# Revit family: QF_BOURGEAT_Self_Bain_marie_air_5GN
name_source: partatom
category: Equipement spécialisé
revit_build: Autodesk Revit 2015 (Build: 20140606_1530(x64)
units: mm (PartAtom-declared; Revit-internal decimal feet)

## types (18) — shared parameters
Certification = NF alimentaire
Charge max = 200.00 kg
Cuve à air = Oui
Cuve à eau = Non
Fabricant = BOURGEAT
Fréquence = 50 Hz
Indice de protection = 21
Longueur hors tout = 1859 mm  [stored 6.09908 ft]
Nature isolant = Laine de verre
Phase = 2
Profondeur hors tout = 820 mm  [stored 2.69029 ft]
Spécification du Fabricant = Bain-marie Oasis
Tension = 230 V
URL catalogue = http://www.bourgeat.fr
lg_etagere = 1387 mm  [stored 4.55052 ft]
lg_porte = 704 mm
lg_presentoir = 1747 mm  [stored 5.73163 ft]
lgconsole = 1815 mm  [stored 5.95472 ft]
lgmeuble = 1791 mm  [stored 5.87598 ft]

## per-type parameters (varying)
| type | Etageres | Hauteur hors tout | Intensité nominale | Modèle | Pieds | Poids net à vide | Presentoir | Puissance électrique  | Reserves | Roues |
| 5GN_baie_libre | Non | 900 mm | 14 A | 851015 | Oui | 190.00 kg | Non | 3300 W | Non | Non |
| 5GN_reserve | Non | 900 mm | 18 A | 851215 | Oui | 190.00 kg | Non | 4200 W | Oui | Non |
| 5GN_baie_libre+roues | Non | 900 mm | 14 A | 851015+854950 | Non | 190.00 kg | Non | 3300 W | Non | Oui |
| 5GN_baie_libre+etageres | Oui | 900 mm | 14 A | 851015+854935 | Oui | 190.00 kg | Non | 3300 W | Non | Non |
| 5GN_baie_libre+presentoir_neutre | Non | 1330 mm | 14 A | 851015+851315 | Oui | 215.00 kg | Oui | 3300 W | Non | Non |
| 5GN_baie_libre+presentoir_chauffant | Non | 1330 mm | 18 A | 851015+851305 | Oui | 215.00 kg | Oui | 4100 W | Non | Non |
| 5GN_baie_libre+roues+etageres | Oui | 900 mm | 14 A | 851015+854950+854935 | Non | 190.00 kg | Non | 3300 W | Non | Oui |
| 5GN_baie_libre+roues+presentoir_neutre | Non | 1330 mm | 14 A | 851015+854950+851315 | Non | 215.00 kg | Oui | 3300 W | Non | Oui |
| 5GN_baie_libre+roues+presentoir_chauffant | Non | 1330 mm | 18 A | 851015+854950+851305 | Non | 215.00 kg | Oui | 4100 W | Non | Oui |
| 5GN_baie_libre+etageres+presentoir_neutre | Oui | 1330 mm | 14 A | 851015+854935+851315 | Oui | 215.00 kg | Oui | 3300 W | Non | Non |
| 5GN_baie_libre+etageres+presentoir_chauffant | Oui | 1330 mm | 18 A | 851015+854935+851305 | Oui | 215.00 kg | Oui | 4100 W | Non | Non |
| 5GN_baie_libre+etageres+presentoir_chauffant+roues | Oui | 1330 mm | 18 A | 851015+854935+851305+854950 | Non | 215.00 kg | Oui | 4100 W | Non | Oui |
| 5GN_baie_libre+etageres+presentoir_neutre+roues | Oui | 1330 mm | 14 A | 851015+854935+851315+854950 | Oui | 215.00 kg | Oui | 3300 W | Non | Non |
| 5GN_reserve+roues | Non | 900 mm | 18 A | 851215+854950 | Non | 190.00 kg | Non | 4200 W | Oui | Oui |
| 5GN_reserve+presentoir_neutre | Non | 1330 mm | 18 A | 851215+851315 | Oui | 215.00 kg | Oui | 4200 W | Oui | Non |
| 5GN_reserve+presentoir_chauffant | Non | 1330 mm | 22 A | 851215+851315 | Oui | 215.00 kg | Oui | 5000 W | Oui | Non |
| 5GN_reserve+roues+presentoir_neutre | Non | 1330 mm | 18 A | 851215+854950+851315 | Non | 215.00 kg | Oui | 4200 W | Oui | Oui |
| 5GN_reserve+roues+presentoir_chauffant | Non | 1330 mm | 22 A | 851215+854950+851305 | Non | 215.00 kg | Oui | 5000 W | Oui | Oui |

note: [stored X ft] marks values corroborated as IEEE doubles in the binary element streams (Revit-internal decimal feet)

## geometry (parser evidence)
native form markers: Blend x12
no freeform markers — native parametric forms only
